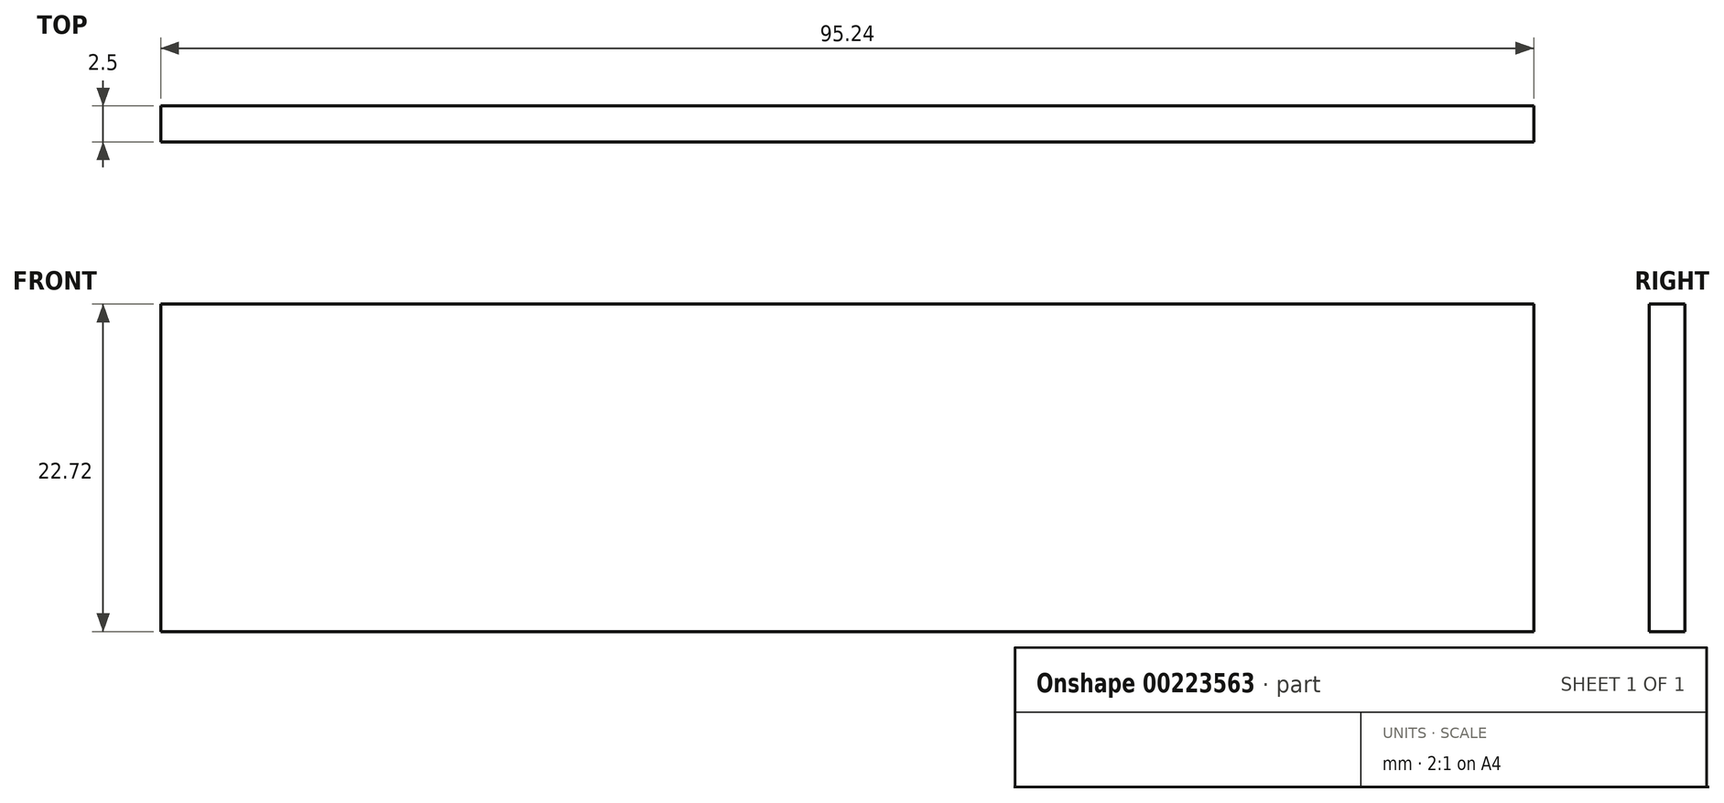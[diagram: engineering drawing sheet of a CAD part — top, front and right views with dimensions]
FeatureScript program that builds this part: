
annotation { "Feature Type Name" : "Feature", "Feature Type Description" : "" }
export const myFeature = defineFeature(function(context is Context, id is Id, definition is map)
    precondition{}
    {
        {
            var Q0;
            Q0=qCreatedBy(makeId("Front.planeOp"),FACE);
            var sketch = newSketch(context, id + "F0", { "sketchPlane" : qUnion([Q0])});
            skLineSegment(sketch, "E0.bottom", {"start": v(47.63, -11.36) * mm, "end": v(-47.63, -11.36) * mm});
            skLineSegment(sketch, "E0.top", {"start": v(47.63, 11.36) * mm, "end": v(-47.63, 11.36) * mm});
            skLineSegment(sketch, "E0.left", {"start": v(47.63, -11.36) * mm, "end": v(47.63, 11.36) * mm});
            skLineSegment(sketch, "E0.right", {"start": v(-47.63, -11.36) * mm, "end": v(-47.63, 11.36) * mm});
            skPoint(sketch, "E0.middle", {"position": v(0, 0) * mm});
            skSolve(sketch);
        }
        {
            var Q0;
            Q0=makeQuery(id+"F0.imprint","IMPRINT",FACE,{"disambiguationData":[TD([[makeQuery(id+"F0.imprint","IMPRINT",EDGE,{"derivedFrom":sQuery(id+"F0.wireOp",EDGE,"E0.bottom")}),-1.0]])]});
            extrude(context, id + "F1", {"entities" : qUnion([Q0]), "depth" : 2.5 * mm});
        }
    });
